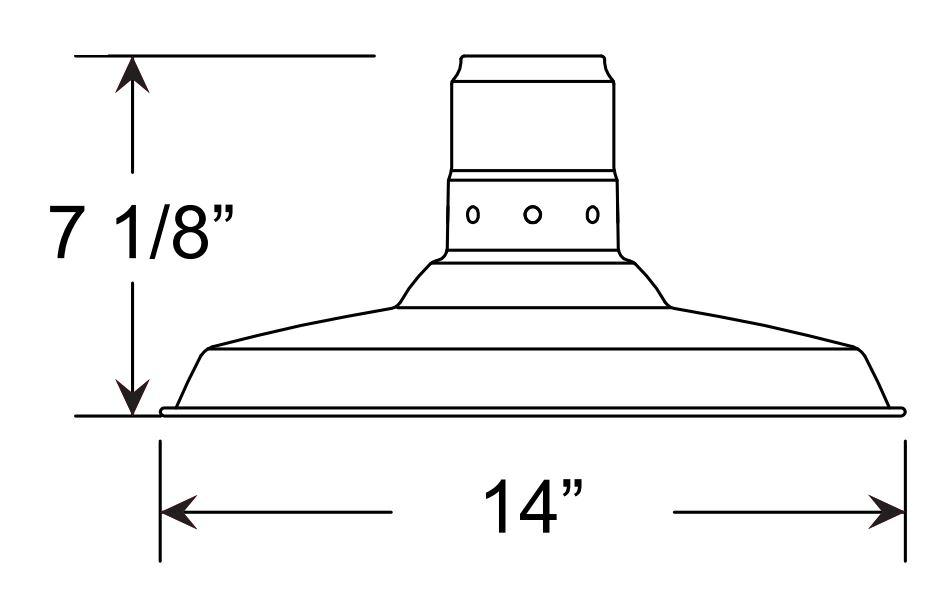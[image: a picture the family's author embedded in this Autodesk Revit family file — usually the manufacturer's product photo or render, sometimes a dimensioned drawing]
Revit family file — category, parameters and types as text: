
# Revit family: Angle_MB
name_source: partatom
category: Lighting Fixtures
units: mm (PartAtom-declared; Revit-internal decimal feet)

## family parameters
Always vertical = Yes
Cut with Voids When Loaded = No
Light Source = Yes
OmniClass Number = 23.80.70.00
OmniClass Title = Lighting
Part Type = Normal
Room Calculation Point = No
Round Connector Dimension = Use Diameter
Shared = No
Work Plane-Based = No

## types (4) — shared parameters
Body Colour = Spun aluminium
Body Material = body
CRI = >90
Canopy Body = body
Color Filter = 16777215
Construction Material = Heavy Duty spun aluminum.
Default Elevation = 0' - 0"
Description = 120-277 Voltage
Dimming = 1%
Dimming Lamp Color Temperature Shift = <None>
Efficiency = 65-125 lumens per watt
Life = L70 50,000 hours
Load Classification = Lighting
Manufacturer = ANP Lighting
Photometric Web File = A812GLCL-42WPL-E3.ies
Power Factor = 1
URL = https://www.anplighting.com
Voltage = 120 V
Warranty = 5 year limited warranty

## per-type parameters (varying)
| type | A807 | A810 | A812 | A814 | Apparent Load | Fixture Diameter | Fixture Height | Lamp | Tilt Angle | Wattage Comments | Weight |
| A807 | Yes | No | No | No | 100 VA | 0' - 7" | 0' - 6 1/2" | 100W MAX MEDIUM BASE | 90.00° | 100W | 1.0 lb |
| A810 | No | Yes | No | No | 100 VA | 0' - 10" | 0' - 8 1/2" | 100W MAX MEDIUM BASE | 90.00° | 100W | 1.0 lb |
| A812 | No | No | Yes | No | 200 VA | 1' - 0" | 0' - 10" | 200W MAX MEDIUM BASE | 60.00° | 200W | 1.0 lb |
| A814 | No | No | No | Yes | 200 VA | 1' - 2 1/2" | 1' - 0" | 200W MAX MEDIUM BASE | 90.00° | 200W | 1.5 lb |

note: column(s) folded — value = type name in every type: Model

## geometry (parser evidence)
native form markers: Sweep x38
no freeform markers — native parametric forms only
